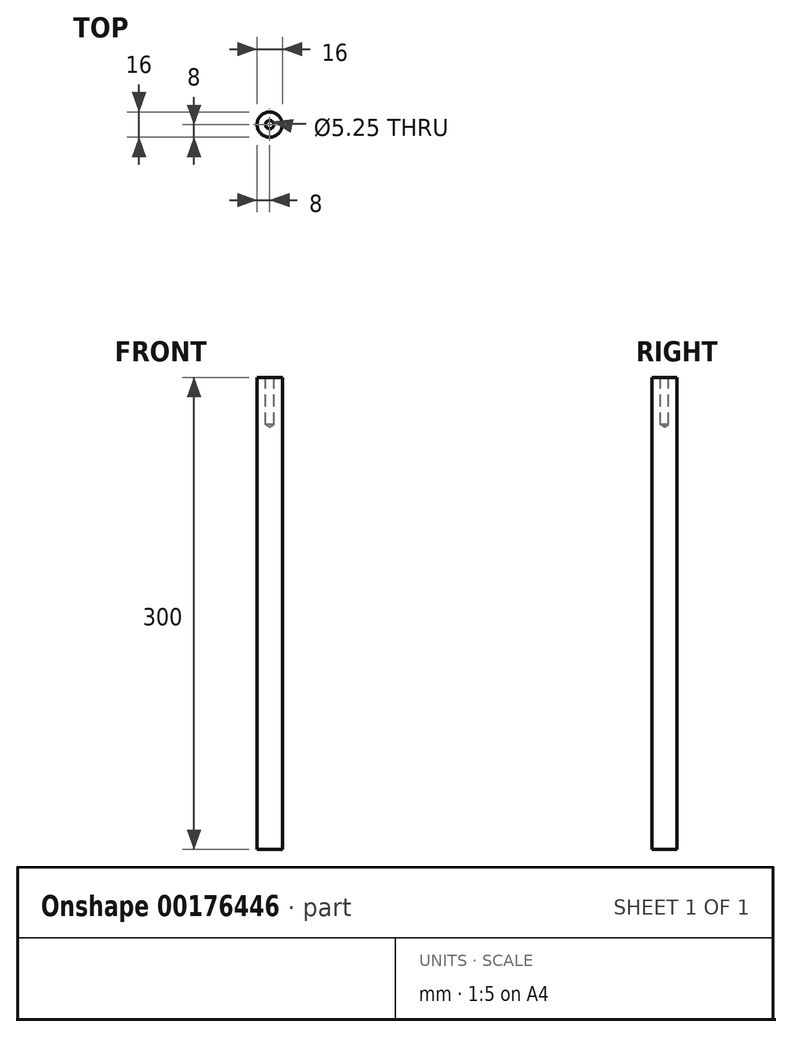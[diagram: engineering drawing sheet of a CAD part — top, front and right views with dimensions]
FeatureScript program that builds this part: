
annotation { "Feature Type Name" : "Feature", "Feature Type Description" : "" }
export const myFeature = defineFeature(function(context is Context, id is Id, definition is map)
    precondition{}
    {
        {
            var Q0;
            Q0=qCreatedBy(makeId("Top.planeOp"),FACE);
            var sketch = newSketch(context, id + "F0", { "sketchPlane" : qUnion([Q0])});
            skCircle(sketch, "E0", {"center": v(0, 0) * mm, "radius": 8 * mm});
            skSolve(sketch);
        }
        {
            var Q0;
            Q0=makeQuery(id+"F0.imprint","IMPRINT",FACE,{"disambiguationData":[TD([[makeQuery(id+"F0.imprint","IMPRINT",EDGE,{"derivedFrom":sQuery(id+"F0.wireOp",EDGE,"E0")}),1.0]])]});
            extrude(context, id + "F1", {"entities" : qUnion([Q0]), "depth" : 300 * mm});
        }
        {
            var Q0;
            Q0=makeQuery(id+"F1.opExtrude","CAP_FACE",FACE,{"disambiguationData":[OSD([sQuery(id+"F0.wireOp",EDGE,"E0")])],"isStart":false});
            var sketch = newSketch(context, id + "F2", { "sketchPlane" : qUnion([Q0])});
            skCircle(sketch, "E1", {"center": v(0, 0) * mm, "radius": 2.9 * mm});
            skSolve(sketch);
        }
        {
            var Q0;
            Q0=sQuery(id+"F2.wireOp",VERTEX,"E1.center");
            var Q1;
            Q1=makeQuery(id+"F1.opExtrude","SWEPT_BODY",BODY,{"disambiguationData":[OSD([sQuery(id+"F0.wireOp",EDGE,"E0")])]});
            hole(context, id + "F3", {"style" : HoleStyle.SIMPLE, "endStyle" : HoleEndStyle.BLIND, "standardTappedOrClearance" : lookupTablePath({ "standard" : "ISO", "engagement" : "75%", "pitch" : "0.75 mm", "size" : "M6", "type" : "Tapped" }), "standardBlindInLast" : lookupTablePath({ "standard" : "ISO", "engagement" : "75%", "pitch" : "0.75 mm", "size" : "M6", "type" : "Tapped" }), "holeDiameter" : 5.25 * mm, "holeDepth" : 30 * mm, "startFromSketch" : true, "locations" : qUnion([Q0]), "scope" : qUnion([Q1]), "majorDiameter" : 6 * mm});
        }
    });
